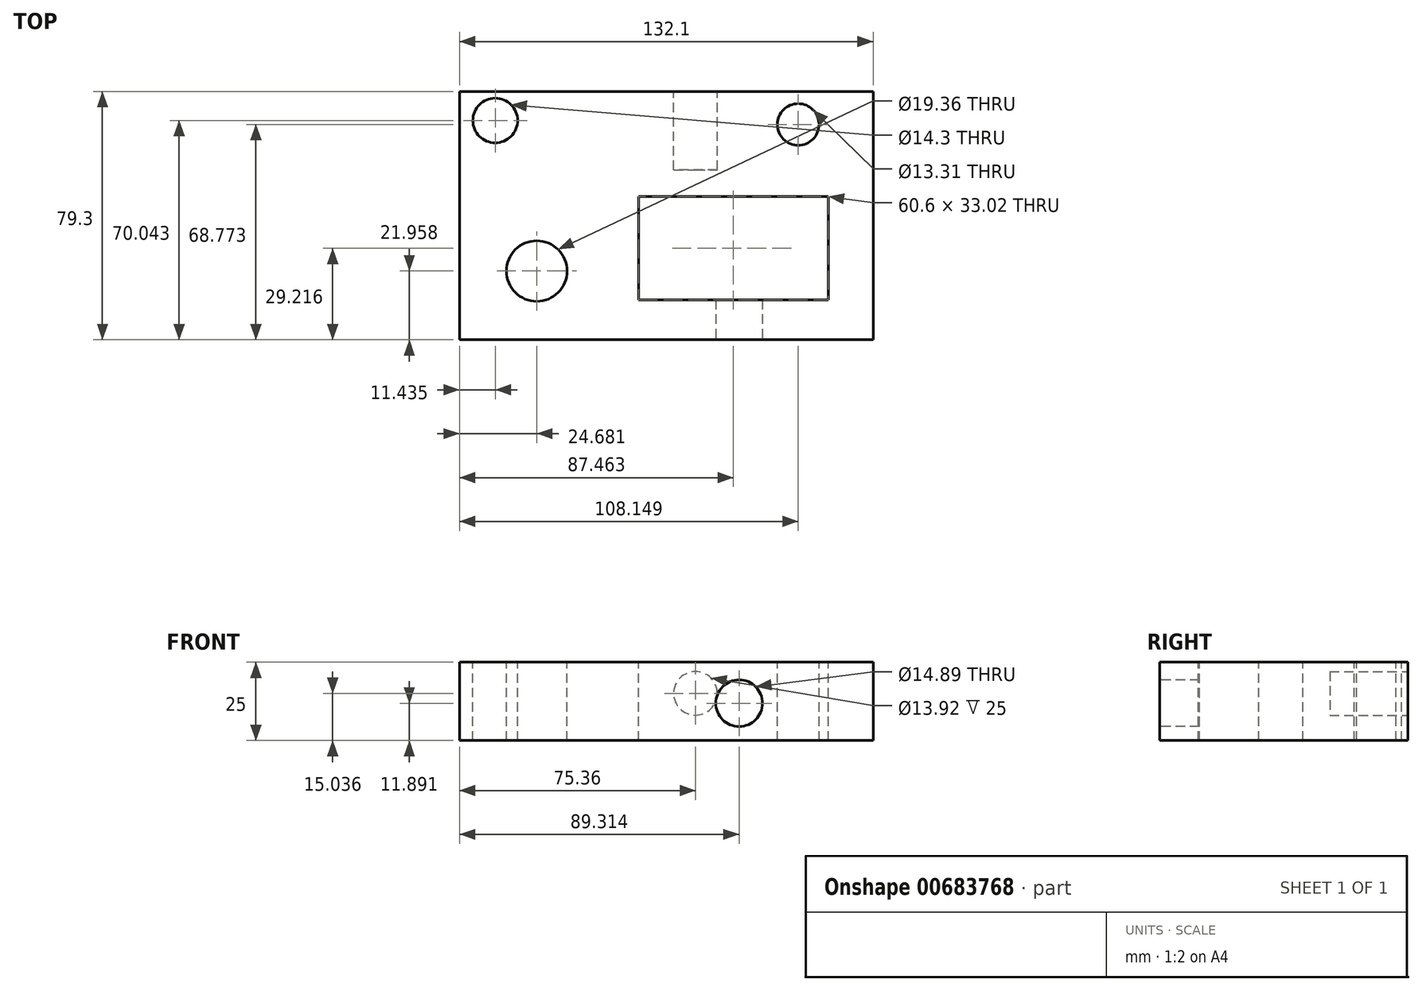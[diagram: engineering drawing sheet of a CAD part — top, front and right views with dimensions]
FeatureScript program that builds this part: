
annotation { "Feature Type Name" : "Feature", "Feature Type Description" : "" }
export const myFeature = defineFeature(function(context is Context, id is Id, definition is map)
    precondition{}
    {
        {
            var Q0;
            Q0=qCreatedBy(makeId("Top.planeOp"),FACE);
            var sketch = newSketch(context, id + "F0", { "sketchPlane" : qUnion([Q0])});
            skLineSegment(sketch, "E0.bottom", {"start": v(-67.05, 37.1) * mm, "end": v(65.05, 37.1) * mm});
            skLineSegment(sketch, "E0.top", {"start": v(-67.05, -42.19) * mm, "end": v(65.05, -42.19) * mm});
            skLineSegment(sketch, "E0.left", {"start": v(-67.05, 37.1) * mm, "end": v(-67.05, -42.19) * mm});
            skLineSegment(sketch, "E0.right", {"start": v(65.05, 37.1) * mm, "end": v(65.05, -42.19) * mm});
            skSolve(sketch);
        }
        {
            var Q0;
            Q0=makeQuery(id+"F0.imprint","IMPRINT",FACE,{"disambiguationData":[TD([[makeQuery(id+"F0.imprint","IMPRINT",EDGE,{"derivedFrom":sQuery(id+"F0.wireOp",EDGE,"E0.bottom")}),-1.0]])]});
            extrude(context, id + "F1", {"entities" : qUnion([Q0]), "depth" : 25 * mm, "offsetDistance" : 25 * mm});
        }
        {
            var Q0;
            Q0=makeQuery(id+"F1.opExtrude","CAP_FACE",FACE,{"disambiguationData":[OSD([sQuery(id+"F0.wireOp",EDGE,"E0.bottom"),sQuery(id+"F0.wireOp",EDGE,"E0.top"),sQuery(id+"F0.wireOp",EDGE,"E0.left"),sQuery(id+"F0.wireOp",EDGE,"E0.right")])],"isStart":false});
            var sketch = newSketch(context, id + "F2", { "sketchPlane" : qUnion([Q0])});
            skCircle(sketch, "E1", {"center": v(-55.61, 27.85) * mm, "radius": 7.15 * mm});
            skCircle(sketch, "E2", {"center": v(-42.37, -20.23) * mm, "radius": 9.68 * mm});
            skCircle(sketch, "E3", {"center": v(41.1, 26.58) * mm, "radius": 6.65 * mm});
            skLineSegment(sketch, "E4.bottom", {"start": v(-9.89, 3.54) * mm, "end": v(50.72, 3.54) * mm});
            skLineSegment(sketch, "E4.top", {"start": v(-9.89, -29.49) * mm, "end": v(50.72, -29.49) * mm});
            skLineSegment(sketch, "E4.left", {"start": v(-9.89, 3.54) * mm, "end": v(-9.89, -29.49) * mm});
            skLineSegment(sketch, "E4.right", {"start": v(50.72, 3.54) * mm, "end": v(50.72, -29.49) * mm});
            skSolve(sketch);
        }
        {
            var Q0;
            Q0=makeQuery(id+"F2.imprint","IMPRINT",FACE,{"disambiguationData":[TD([[makeQuery(id+"F2.imprint","IMPRINT",EDGE,{"derivedFrom":sQuery(id+"F2.wireOp",EDGE,"E1")}),1.0]])]});
            var Q1;
            Q1=makeQuery(id+"F2.imprint","IMPRINT",FACE,{"disambiguationData":[TD([[makeQuery(id+"F2.imprint","IMPRINT",EDGE,{"derivedFrom":sQuery(id+"F2.wireOp",EDGE,"E2")}),1.0]])]});
            extrude(context, id + "F3", {"entities" : qUnion([Q0, Q1]), "operationType" : NewBodyOperationType.REMOVE, "oppositeDirection" : true, "depth" : 25 * mm, "offsetDistance" : 25 * mm});
        }
        {
            var Q0;
            Q0 = qSketchRegion(id + "F2", true);
            extrude(context, id + "F4", {"entities" : qUnion([Q0]), "operationType" : NewBodyOperationType.REMOVE, "oppositeDirection" : true, "depth" : 25 * mm, "offsetDistance" : 25 * mm});
        }
        {
            var Q0;
            Q0=makeQuery(id+"F1.opExtrude","SWEPT_FACE",FACE,{"disambiguationData":[OSD([sQuery(id+"F0.wireOp",EDGE,"E0.top")])]});
            var sketch = newSketch(context, id + "F5", { "sketchPlane" : qUnion([Q0])});
            skCircle(sketch, "E5", {"center": v(22.26, 11.9) * mm, "radius": 7.45 * mm});
            skSolve(sketch);
        }
        {
            var Q0;
            Q0=makeQuery(id+"F5.imprint","IMPRINT",FACE,{"disambiguationData":[TD([[makeQuery(id+"F5.imprint","IMPRINT",EDGE,{"derivedFrom":sQuery(id+"F5.wireOp",EDGE,"E5")}),1.0]])]});
            extrude(context, id + "F6", {"entities" : qUnion([Q0]), "operationType" : NewBodyOperationType.REMOVE, "oppositeDirection" : true, "depth" : 25 * mm, "offsetDistance" : 25 * mm});
        }
        {
            var Q0;
            Q0=makeQuery(id+"F1.opExtrude","SWEPT_FACE",FACE,{"disambiguationData":[OSD([sQuery(id+"F0.wireOp",EDGE,"E0.bottom")])]});
            var sketch = newSketch(context, id + "F7", { "sketchPlane" : qUnion([Q0])});
            skCircle(sketch, "E6", {"center": v(-8.31, 15.04) * mm, "radius": 6.96 * mm});
            skSolve(sketch);
        }
        {
            var Q0;
            Q0=makeQuery(id+"F7.imprint","IMPRINT",FACE,{"disambiguationData":[TD([[makeQuery(id+"F7.imprint","IMPRINT",EDGE,{"derivedFrom":sQuery(id+"F7.wireOp",EDGE,"E6")}),1.0]])]});
            extrude(context, id + "F8", {"entities" : qUnion([Q0]), "operationType" : NewBodyOperationType.REMOVE, "oppositeDirection" : true, "depth" : 25 * mm, "offsetDistance" : 25 * mm});
        }
    });
